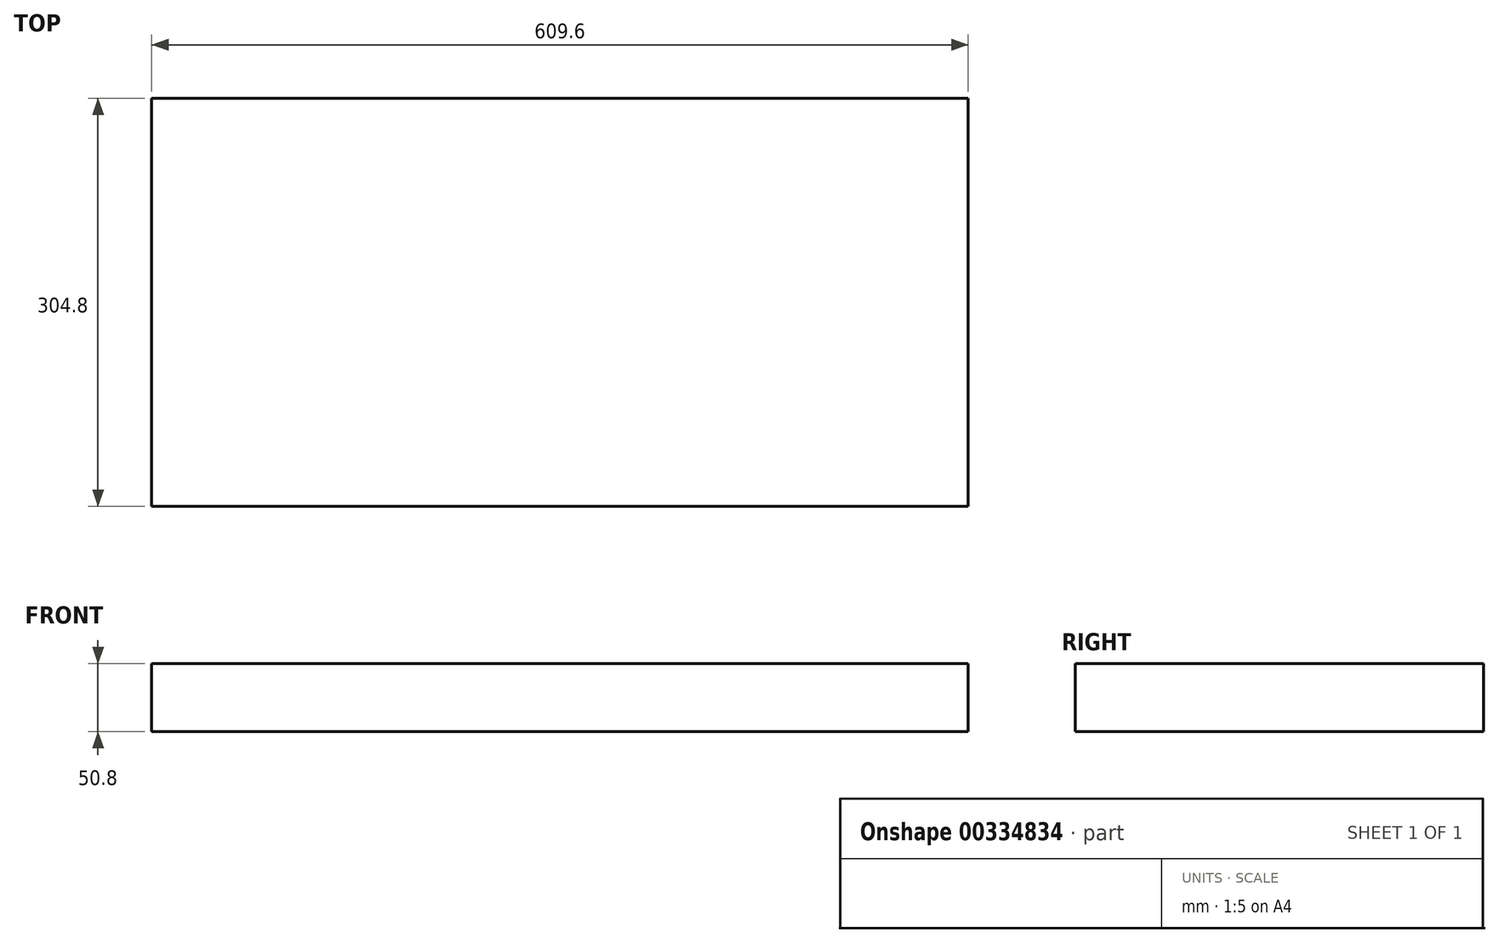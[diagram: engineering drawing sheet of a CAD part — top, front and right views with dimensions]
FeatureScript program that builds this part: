
annotation { "Feature Type Name" : "Feature", "Feature Type Description" : "" }
export const myFeature = defineFeature(function(context is Context, id is Id, definition is map)
    precondition{}
    {
        {
            var Q0;
            Q0=qCreatedBy(makeId("Top.planeOp"),FACE);
            var sketch = newSketch(context, id + "F0", { "sketchPlane" : qUnion([Q0])});
            skLineSegment(sketch, "E0.bottom", {"start": v(-151.25, 233.54) * mm, "end": v(458.35, 233.54) * mm});
            skLineSegment(sketch, "E0.top", {"start": v(-151.25, -71.26) * mm, "end": v(458.35, -71.26) * mm});
            skLineSegment(sketch, "E0.left", {"start": v(-151.25, 233.54) * mm, "end": v(-151.25, -71.26) * mm});
            skLineSegment(sketch, "E0.right", {"start": v(458.35, 233.54) * mm, "end": v(458.35, -71.26) * mm});
            skSolve(sketch);
        }
        {
            var Q0;
            Q0=makeQuery(id+"F0.imprint","IMPRINT",FACE,{"disambiguationData":[TD([[makeQuery(id+"F0.imprint","IMPRINT",EDGE,{"derivedFrom":sQuery(id+"F0.wireOp",EDGE,"E0.bottom")}),-1.0]])]});
            extrude(context, id + "F1", {"entities" : qUnion([Q0]), "depth" : 50.8 * mm});
        }
    });
